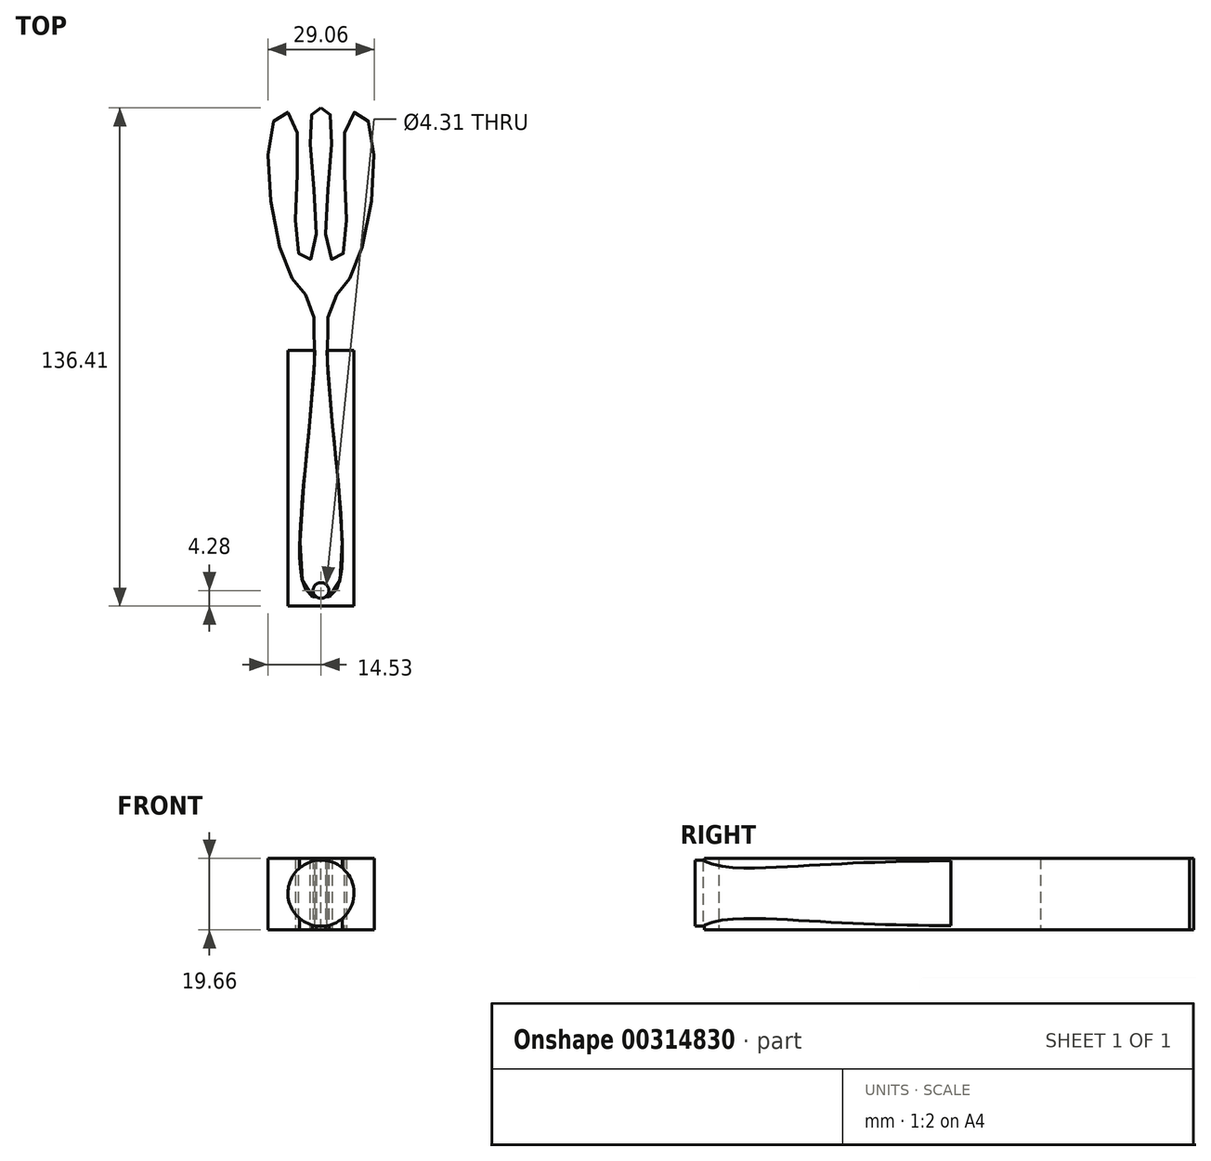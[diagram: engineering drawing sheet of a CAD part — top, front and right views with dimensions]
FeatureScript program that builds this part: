
annotation { "Feature Type Name" : "Feature", "Feature Type Description" : "" }
export const myFeature = defineFeature(function(context is Context, id is Id, definition is map)
    precondition{}
    {
        {
            var Q0;
            Q0=qCreatedBy(makeId("Top.planeOp"),FACE);
            var sketch = newSketch(context, id + "F0", { "sketchPlane" : qUnion([Q0])});
            skLineSegment(sketch, "E0.bottom", {"start": v(-32.92, 70.52) * mm, "end": v(32.92, 70.52) * mm});
            skLineSegment(sketch, "E0.top", {"start": v(-32.92, -70.52) * mm, "end": v(32.92, -70.52) * mm});
            skLineSegment(sketch, "E0.left", {"start": v(-32.92, 70.52) * mm, "end": v(-32.92, -70.52) * mm});
            skLineSegment(sketch, "E0.right", {"start": v(32.92, 70.52) * mm, "end": v(32.92, -70.52) * mm});
            skPoint(sketch, "E0.middle", {"position": v(0, 0) * mm});
            skSolve(sketch);
        }
        {
            var Q0;
            Q0=makeQuery(id+"F0.imprint","IMPRINT",FACE,{"disambiguationData":[TD([[makeQuery(id+"F0.imprint","IMPRINT",EDGE,{"derivedFrom":sQuery(id+"F0.wireOp",EDGE,"E0.bottom")}),-1.0]])]});
            extrude(context, id + "F1", {"entities" : qUnion([Q0]), "depth" : 30 * mm});
        }
        {
            var Q0;
            Q0=makeQuery(id+"F1.opExtrude","CAP_FACE",FACE,{"disambiguationData":[OSD([sQuery(id+"F0.wireOp",EDGE,"E0.bottom"),sQuery(id+"F0.wireOp",EDGE,"E0.top"),sQuery(id+"F0.wireOp",EDGE,"E0.left"),sQuery(id+"F0.wireOp",EDGE,"E0.right")])],"isStart":false});
            var sketch = newSketch(context, id + "F2", { "sketchPlane" : qUnion([Q0])});
            skFitSpline(sketch, "E1", {"points": [v(0, 66.4) * mm, v(2.74, 63.9) * mm, v(2.29, 25.72) * mm, v(5.94, 26.17) * mm, v(7.54, 63.66) * mm, v(12.57, 63.43) * mm, v(8.92, 21.6) * mm, v(2.06, 9.94) * mm, v(5.26, -62.52) * mm, v(0, -68.46) * mm], "startDerivative": vector(70.08, -13.33) * mm, "endDerivative": vector(-91.97, -34.22) * mm});
            skLineSegment(sketch, "E2", {"start": v(0, 66.4) * mm, "end": v(0, -68.46) * mm});
            skFitSpline(sketch, "E3.MirrorCS", {"points": [v(0, 66.4) * mm, v(-2.74, 63.9) * mm, v(-2.29, 25.72) * mm, v(-5.94, 26.17) * mm, v(-7.54, 63.66) * mm, v(-12.57, 63.43) * mm, v(-8.92, 21.6) * mm, v(-2.06, 9.94) * mm, v(-5.26, -62.52) * mm, v(0, -68.46) * mm], "startDerivative": vector(-70.08, -13.33) * mm, "endDerivative": vector(91.97, -34.22) * mm});
            skSolve(sketch);
        }
        {
            var Q0;
            Q0=makeQuery(id+"F1.opExtrude","SWEPT_FACE",FACE,{"disambiguationData":[OSD([sQuery(id+"F0.wireOp",EDGE,"E0.right")])]});
            var sketch = newSketch(context, id + "F3", { "sketchPlane" : qUnion([Q0])});
            skLineSegment(sketch, "E4.bottom", {"start": v(0, 30) * mm, "end": v(0, 30) * mm});
            skLineSegment(sketch, "E4.top", {"start": v(0, -30) * mm, "end": v(0, -30) * mm});
            skLineSegment(sketch, "E4.left", {"start": v(0, 30) * mm, "end": v(0, -30) * mm});
            skLineSegment(sketch, "E4.right", {"start": v(0, 30) * mm, "end": v(0, -30) * mm});
            skPoint(sketch, "E4.middle", {"position": v(0, 0) * mm});
            skLineSegment(sketch, "E5.bottom", {"start": v(-67.43, 7.66) * mm, "end": v(67.43, 7.66) * mm});
            skLineSegment(sketch, "E5.top", {"start": v(-67.43, 27.32) * mm, "end": v(67.43, 27.32) * mm});
            skLineSegment(sketch, "E5.left", {"start": v(-67.43, 7.66) * mm, "end": v(-67.43, 27.32) * mm});
            skLineSegment(sketch, "E5.right", {"start": v(67.43, 7.66) * mm, "end": v(67.43, 27.32) * mm});
            skPoint(sketch, "E5.middle", {"position": v(0, 17.49) * mm});
            skPoint(sketch, "E6.5.internal.snap0", {"position": v(-67.43, 17.49) * mm});
            skFitSpline(sketch, "E6", {"points": [v(67.43, 21.83) * mm, v(54.4, 20) * mm, v(27.66, 23.2) * mm, v(-67.43, 17.49) * mm, v(-62.86, 12.46) * mm, v(-55.55, 17.49) * mm, v(22.17, 17.49) * mm, v(49.83, 15.2) * mm, v(67.43, 21.83) * mm]});
            skSolve(sketch);
        }
        {
            var Q0;
            {var subQ7=sQuery(id+"F0.wireOp",EDGE,"E0.right");var subQ11=makeQuery(id+"F1.opExtrude","SWEPT_EDGE",EDGE,{"disambiguationData":[OSD([sQuery(id+"F0.wireOp",EDGE,"E0.top"),subQ7])]});Q0=makeQuery(id+"F3.imprint","IMPRINT",FACE,{"disambiguationData":[TD([[makeQuery(id+"F3.imprint","IMPRINT",EDGE,{"derivedFrom":subQ11}),1.0]])]});}
            var Q1;
            {var subQ8=sQuery(id+"F0.wireOp",EDGE,"E0.right");var subQ15=makeQuery(id+"F1.opExtrude","SWEPT_EDGE",EDGE,{"disambiguationData":[OSD([sQuery(id+"F0.wireOp",EDGE,"E0.bottom"),subQ8])]});Q1=makeQuery(id+"F3.imprint","IMPRINT",FACE,{"disambiguationData":[TD([[makeQuery(id+"F3.imprint","IMPRINT",EDGE,{"derivedFrom":subQ15}),-1.0]])]});}
            var Q2;
            {var subQ0=sQuery(id+"F3.wireOp",EDGE,"E6");var subQ1=sQuery(id+"F3.wireOp",EDGE,"E4.right");var subQ2=makeQuery(id+"F3.imprint","INTERSECT",VERTEX,{"disambiguationData":[OD(1.0)],"derivedFrom":[subQ1,subQ0]});Q2=makeQuery(id+"F3.imprint","IMPRINT",FACE,{"disambiguationData":[TD([[makeQuery(id+"F3.imprint","IMPRINT",EDGE,{"disambiguationData":[TD([[subQ2,-1.0]])],"derivedFrom":subQ1}),-1.0]])]});}
            var Q3;
            {var subQ0=sQuery(id+"F3.wireOp",EDGE,"E6");var subQ1=sQuery(id+"F3.wireOp",EDGE,"E4.right");var subQ2=makeQuery(id+"F3.imprint","INTERSECT",VERTEX,{"disambiguationData":[OD(1.0)],"derivedFrom":[subQ1,subQ0]});Q3=makeQuery(id+"F3.imprint","IMPRINT",FACE,{"disambiguationData":[TD([[makeQuery(id+"F3.imprint","IMPRINT",EDGE,{"disambiguationData":[TD([[subQ2,-1.0]])],"derivedFrom":subQ1}),1.0]])]});}
            var Q4;
            {var subQ0=sQuery(id+"F3.wireOp",EDGE,"E5.top");var subQ1=sQuery(id+"F3.wireOp",EDGE,"E4.right");var subQ2=makeQuery(id+"F3.imprint","INTERSECT",VERTEX,{"derivedFrom":[subQ1,subQ0]});Q4=makeQuery(id+"F3.imprint","IMPRINT",FACE,{"disambiguationData":[TD([[makeQuery(id+"F3.imprint","IMPRINT",EDGE,{"disambiguationData":[TD([[subQ2,-1.0]])],"derivedFrom":subQ1}),1.0]])]});}
            var Q5;
            {var subQ0=sQuery(id+"F3.wireOp",EDGE,"E5.top");var subQ1=sQuery(id+"F3.wireOp",EDGE,"E4.right");var subQ2=makeQuery(id+"F3.imprint","INTERSECT",VERTEX,{"derivedFrom":[subQ1,subQ0]});Q5=makeQuery(id+"F3.imprint","IMPRINT",FACE,{"disambiguationData":[TD([[makeQuery(id+"F3.imprint","IMPRINT",EDGE,{"disambiguationData":[TD([[subQ2,-1.0]])],"derivedFrom":subQ1}),-1.0]])]});}
            extrude(context, id + "F4", {"entities" : qUnion([Q0, Q1, Q2, Q3, Q4, Q5]), "operationType" : NewBodyOperationType.REMOVE, "oppositeDirection" : true, "depth" : 30 * mm});
        }
        {
            var Q0;
            Q0=makeQuery(id+"F4.boolean.opBoolean","COPY",FACE,{"derivedFrom":makeQuery(id+"F4.opExtrude","CAP_FACE",FACE,{"disambiguationData":[OSD([sQuery(id+"F0.wireOp",EDGE,"E0.bottom"),sQuery(id+"F0.wireOp",EDGE,"E0.top"),sQuery(id+"F0.wireOp",EDGE,"E0.right"),sQuery(id+"F3.wireOp",EDGE,"E6")])],"isStart":false})});
            extrude(context, id + "F5", {"entities" : qUnion([Q0]), "operationType" : NewBodyOperationType.REMOVE, "oppositeDirection" : true, "depth" : 30 * mm});
        }
        {
            var Q0;
            Q0=makeQuery(id+"F5.boolean.opBoolean","COPY",FACE,{"derivedFrom":makeQuery(id+"F5.opExtrude","CAP_FACE",FACE,{"disambiguationData":[OSD([sQuery(id+"F0.wireOp",EDGE,"E0.bottom"),sQuery(id+"F0.wireOp",EDGE,"E0.top"),sQuery(id+"F0.wireOp",EDGE,"E0.right"),sQuery(id+"F3.wireOp",EDGE,"E6")])],"isStart":false})});
            extrude(context, id + "F6", {"entities" : qUnion([Q0]), "operationType" : NewBodyOperationType.REMOVE, "oppositeDirection" : true, "depth" : 30 * mm});
        }
        {
            var Q0;
            Q0=makeQuery(id+"F2.imprint","IMPRINT",FACE,{"disambiguationData":[TD([[makeQuery(id+"F2.imprint","IMPRINT",EDGE,{"derivedFrom":sQuery(id+"F2.wireOp",EDGE,"E1")}),1.0]])]});
            extrude(context, id + "F7", {"entities" : qUnion([Q0]), "operationType" : NewBodyOperationType.REMOVE, "oppositeDirection" : true, "depth" : 30 * mm});
        }
        {
            var Q0;
            Q0=qCreatedBy(makeId("Front.planeOp"),FACE);
            var sketch = newSketch(context, id + "F8", { "sketchPlane" : qUnion([Q0])});
            skCircle(sketch, "E7", {"center": v(0, 17.72) * mm, "radius": 9.05 * mm});
            skSolve(sketch);
        }
        {
            var Q0;
            Q0 = qSketchRegion(id + "F8", true);
            extrude(context, id + "F9", {"entities" : qUnion([Q0]), "operationType" : NewBodyOperationType.ADD, "depth" : 70 * mm});
        }
        {
            var Q0;
            Q0=qCreatedBy(makeId("Top.planeOp"),FACE);
            var sketch = newSketch(context, id + "F10", { "sketchPlane" : qUnion([Q0])});
            skCircle(sketch, "E8", {"center": v(0, -65.72) * mm, "radius": 2.16 * mm});
            skSolve(sketch);
        }
        {
            var Q0;
            Q0 = qSketchRegion(id + "F10", true);
            extrude(context, id + "F11", {"entities" : qUnion([Q0]), "operationType" : NewBodyOperationType.REMOVE, "depth" : 30 * mm});
        }
    });
